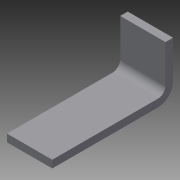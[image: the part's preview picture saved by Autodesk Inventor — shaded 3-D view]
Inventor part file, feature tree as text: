
AUTODESK INVENTOR PART (.ipt)
format: ipt  version: 2013 (Build 170138000, 138)  size: 93,696 bytes
history: native  units: in
note: dims shown in document units (in); Inventor stores cm internally (conversion verified against a paired STEP export)
features: sheet_metal_op x4, sketch x2, other x2
ambient origin geometry x8: Origin, YZ Plane, XZ Plane, XY Plane, X Axis, Y Axis, Z Axis, Center Point
bodies: Solid1 (feature_tree)
feature tree (8):
  sheet_metal_op  "Face1"
  sheet_metal_op  "Flange1"
  sketch  "Sketch1"  dims[d0=0.875in]
  other  "Plate1"
  sketch  "Sketch2"  dims[d1=0.75in d2=0.125in d3=0.125in d4=0.0625in d5=0.25in d6=0.125in d7=2.0in d8=90.0deg d9=0.125in d10=0.5in d11=0.125in d12=0.125in]
  other  "Plate2"
  sheet_metal_op  "Bend1"
  sheet_metal_op  "Corner1"
